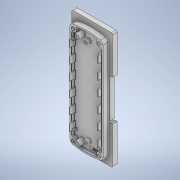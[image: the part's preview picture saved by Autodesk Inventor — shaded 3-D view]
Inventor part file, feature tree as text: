
AUTODESK INVENTOR PART (.ipt)
format: ipt  version: 2021 (Build 250183000, 183)  size: 1,079,808 bytes
history: native  units: mm
features: other x3, sketch x1
ambient origin geometry x8: Origin, YZ Plane, XZ Plane, XY Plane, X Axis, Y Axis, Z Axis, Center Point
bodies: Solid1 (feature_tree)
feature tree (4):
  other  "PanelJigAssembly.iam"
  other  "PanelJig.ipt:1"
  other  "1009799_3D.ipt:1"
  sketch  "Sketch1"  dims[d0=10.0mm]
